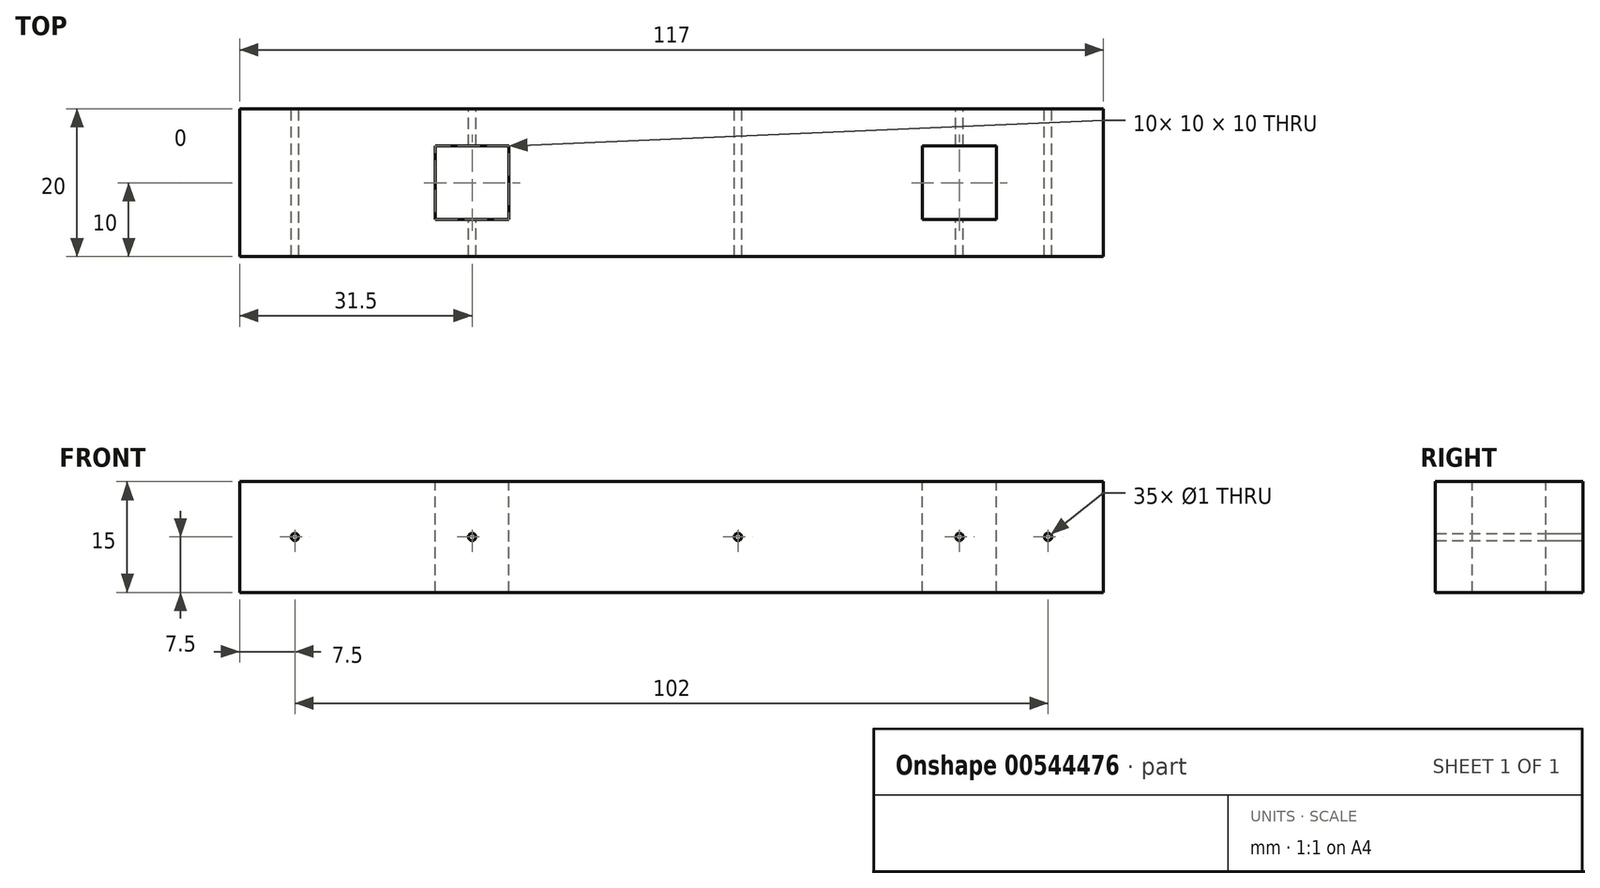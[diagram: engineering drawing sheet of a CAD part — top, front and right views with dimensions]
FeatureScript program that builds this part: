
annotation { "Feature Type Name" : "Feature", "Feature Type Description" : "" }
export const myFeature = defineFeature(function(context is Context, id is Id, definition is map)
    precondition{}
    {
        {
            var Q0;
            Q0=qCreatedBy(makeId("Front.planeOp"),FACE);
            var sketch = newSketch(context, id + "F0", { "sketchPlane" : qUnion([Q0])});
            skLineSegment(sketch, "E0.bottom", {"start": v(0, 0) * mm, "end": v(146, 0) * mm});
            skLineSegment(sketch, "E0.top", {"start": v(0, 31) * mm, "end": v(146, 31) * mm});
            skLineSegment(sketch, "E0.left", {"start": v(0, 0) * mm, "end": v(0, 31) * mm});
            skLineSegment(sketch, "E0.right", {"start": v(146, 0) * mm, "end": v(146, 31) * mm});
            skCircle(sketch, "E1", {"center": v(16, 12) * mm, "radius": 0.5 * mm});
            skCircle(sketch, "E2", {"center": v(76, 12) * mm, "radius": 0.5 * mm});
            skCircle(sketch, "E3", {"center": v(118, 12) * mm, "radius": 0.5 * mm});
            skLineSegment(sketch, "E4", {"start": v(0, 12) * mm, "end": v(146, 12) * mm, "construction": true});
            skCircle(sketch, "E5", {"center": v(40, 12) * mm, "radius": 0.5 * mm});
            skCircle(sketch, "E6", {"center": v(106, 12) * mm, "radius": 0.5 * mm});
            skLineSegment(sketch, "E7.bottom", {"start": v(8.5, 19.5) * mm, "end": v(125.5, 19.5) * mm});
            skLineSegment(sketch, "E7.top", {"start": v(8.5, 4.5) * mm, "end": v(125.5, 4.5) * mm});
            skLineSegment(sketch, "E7.left", {"start": v(8.5, 19.5) * mm, "end": v(8.5, 4.5) * mm});
            skLineSegment(sketch, "E7.right", {"start": v(125.5, 19.5) * mm, "end": v(125.5, 4.5) * mm});
            skPoint(sketch, "E7.middle", {"position": v(67, 12) * mm});
            skSolve(sketch);
        }
        {
            var Q0;
            Q0=makeQuery(id+"F0.imprint","IMPRINT",FACE,{"disambiguationData":[TD([[makeQuery(id+"F0.imprint","IMPRINT",EDGE,{"derivedFrom":sQuery(id+"F0.wireOp",EDGE,"E1")}),-1.0]])]});
            extrude(context, id + "F1", {"entities" : qUnion([Q0]), "depth" : 20 * mm, "offsetDistance" : 25 * mm});
        }
        {
            var Q0;
            Q0=makeQuery(id+"F1.opExtrude","SWEPT_FACE",FACE,{"disambiguationData":[OSD([sQuery(id+"F0.wireOp",EDGE,"E7.bottom")])]});
            var sketch = newSketch(context, id + "F2", { "sketchPlane" : qUnion([Q0])});
            skLineSegment(sketch, "E8", {"start": v(0, -10) * mm, "end": v(146, -10) * mm, "construction": true});
            skLineSegment(sketch, "E9", {"start": v(16, 0) * mm, "end": v(16, -20) * mm, "construction": true});
            skLineSegment(sketch, "E10", {"start": v(76, 0) * mm, "end": v(76, -20) * mm, "construction": true});
            skLineSegment(sketch, "E11", {"start": v(118, 0) * mm, "end": v(118, -20) * mm, "construction": true});
            skLineSegment(sketch, "E12.bottom", {"start": v(35, -5) * mm, "end": v(45, -5) * mm});
            skLineSegment(sketch, "E12.top", {"start": v(35, -15) * mm, "end": v(45, -15) * mm});
            skLineSegment(sketch, "E12.left", {"start": v(35, -5) * mm, "end": v(35, -15) * mm});
            skLineSegment(sketch, "E12.right", {"start": v(45, -5) * mm, "end": v(45, -15) * mm});
            skPoint(sketch, "E12.middle", {"position": v(40, -10) * mm});
            skLineSegment(sketch, "E13.bottom", {"start": v(101, -5) * mm, "end": v(111, -5) * mm});
            skLineSegment(sketch, "E13.top", {"start": v(101, -15) * mm, "end": v(111, -15) * mm});
            skLineSegment(sketch, "E13.left", {"start": v(101, -5) * mm, "end": v(101, -15) * mm});
            skLineSegment(sketch, "E13.right", {"start": v(111, -5) * mm, "end": v(111, -15) * mm});
            skPoint(sketch, "E13.middle", {"position": v(106, -10) * mm});
            skSolve(sketch);
        }
        {
            var Q0;
            Q0=makeQuery(id+"F2.imprint","IMPRINT",FACE,{"disambiguationData":[TD([[makeQuery(id+"F2.imprint","IMPRINT",EDGE,{"derivedFrom":sQuery(id+"F2.wireOp",EDGE,"E12.bottom")}),-1.0]])]});
            var Q1;
            Q1=makeQuery(id+"F2.imprint","IMPRINT",FACE,{"disambiguationData":[TD([[makeQuery(id+"F2.imprint","IMPRINT",EDGE,{"derivedFrom":sQuery(id+"F2.wireOp",EDGE,"E13.bottom")}),-1.0]])]});
            extrude(context, id + "F3", {"entities" : qUnion([Q0, Q1]), "operationType" : NewBodyOperationType.REMOVE, "oppositeDirection" : true, "depth" : 37 * mm, "offsetDistance" : 25 * mm});
        }
    });
